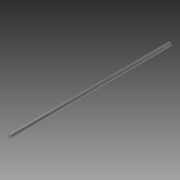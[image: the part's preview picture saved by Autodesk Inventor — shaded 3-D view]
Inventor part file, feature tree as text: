
AUTODESK INVENTOR PART (.ipt)
format: ipt  version: 2014 (Build 180170000, 170)  size: 96,256 bytes
history: native  units: in
note: dims shown in document units (in); Inventor stores cm internally (conversion verified against a paired STEP export)
features: extrude x1, sketch x1
ambient origin geometry x8: Origin, YZ Plane, XZ Plane, XY Plane, X Axis, Y Axis, Z Axis, Center Point
bodies: Solid1 (feature_tree)
feature tree (2):
  extrude  "Extrusion1"  Depth=25.0in TaperAngle=0.0deg
  sketch  "Sketch1"  dims[d0=0.5in d1=25.0in d2=0.0in]
